# Revit family: Bathtub-Freestanding-DXV-Belshire-D12040004.415
name_source: partatom
category: Plumbing Fixtures
revit_build: Autodesk Revit 2016 (Build: 20150714_1515(x64)
units: mm (PartAtom-declared; Revit-internal decimal feet)

## family parameters
Always vertical = No
Cut with Voids When Loaded = No
OmniClass Number = 23.45.05.14.21
OmniClass Title = Bathtubs
Part Type = Normal
Room Calculation Point = No
Round Connector Dimension = Use Radius
Shared = Yes
Work Plane-Based = Yes

## types (1)
- D12040004.415
    Assembly Code = D2010510
    CW Connection = No
    CWFU = 3
    Default Elevation = 0"
    Description = DXV BELSHIRE™ FREESTANDING SOAKING TUB
    Finish = Acrylic-DXC-415-Canvas White
    HW Connection = No
    HWFU = 3
    Height = 24"
    Installation Type = FREESTANDING Floor Mounted
    Length = 36"
    Manufacturer = DXV
    Material = Acrylic-DXC-415-Canvas White
    Model = D12040004.415
    URL = https://www.dxv.com
    Vent Connection = No
    WFU = 4
    Warranty Documentation Link = https://dxv01.blob.core.windows.net
    Waste Connection = Yes
    Waste Connection Diameter = 1 1/2"
    Waste Connection Radius = 1"
    Width = 66"

## geometry (parser evidence)
native form markers: Sweep x2
no freeform markers — native parametric forms only
